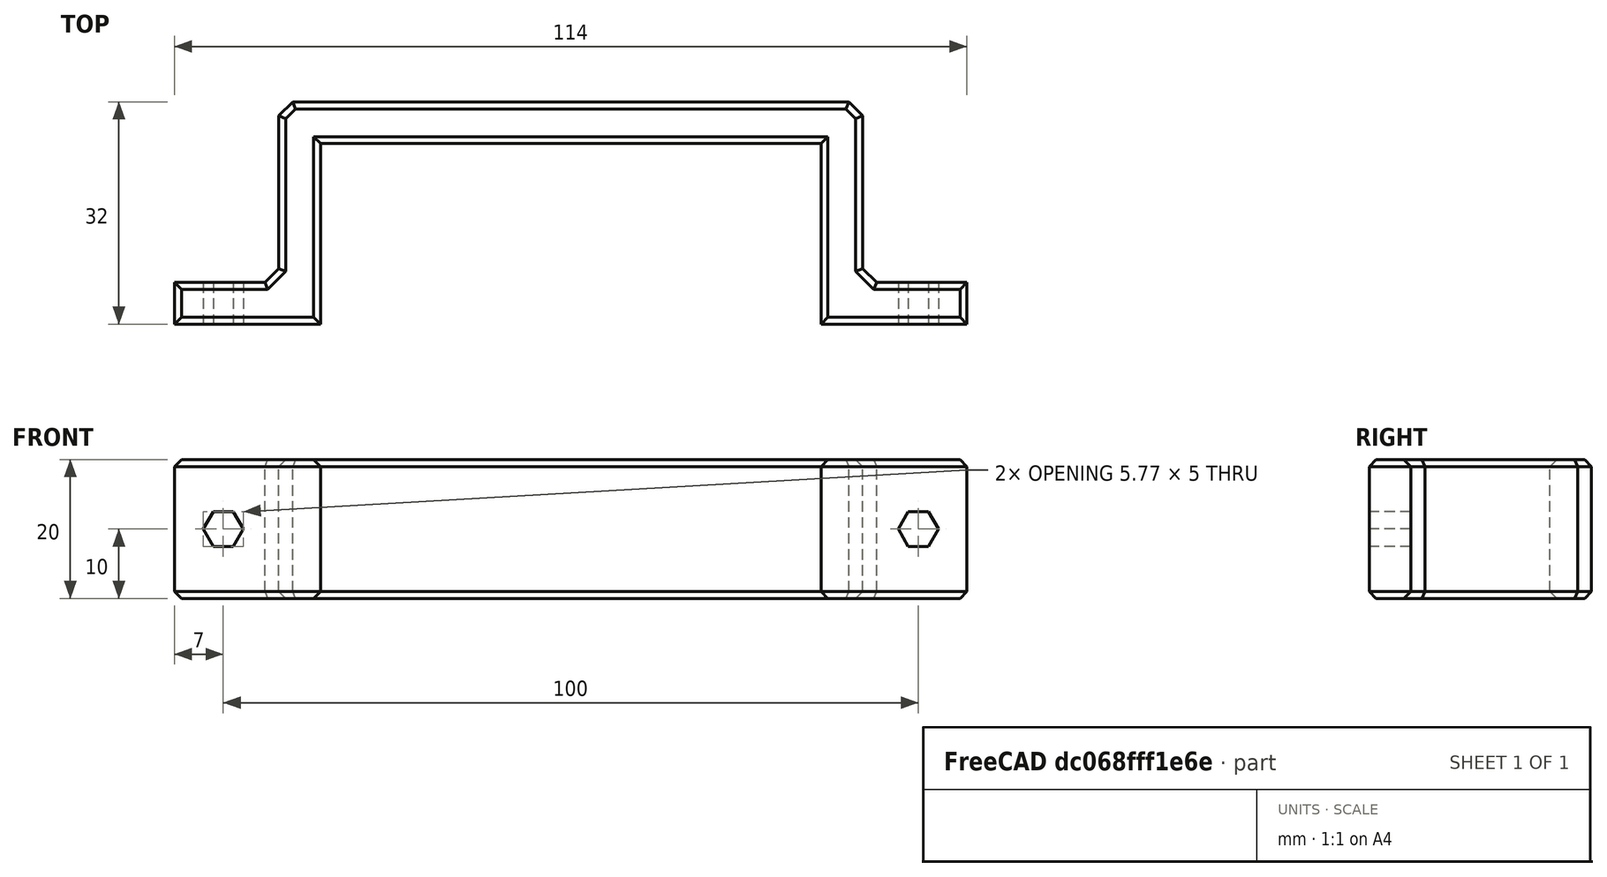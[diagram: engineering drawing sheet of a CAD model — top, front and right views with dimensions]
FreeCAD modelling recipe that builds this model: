
FCSTD DOCUMENT  (FreeCAD 0.19R)
Label: ChargerClip
License: All rights reserved
LicenseURL: http://en.wikipedia.org/wiki/All_rights_reserved
objects: PartDesign::Chamfer×3, Sketcher::SketchObject×2, PartDesign::Pad×1, PartDesign::Pocket×1, PartDesign::Body×1, Mesh::Feature×1
note: 13 computed .brp shape members not serialized (recipe doc carries the construction recipe); baked Part::Feature solids carry a one-line shape summary decoded from their .brp

FEATURE [Sketcher::SketchObject] Sketch
  FullyConstrained = true
  MapMode = 5
  Support = -> [XY_Plane]
  sketch-geometry (12):
    g0: LineSegment StartX=-57 StartY=0 StartZ=0 EndX=-57 EndY=6 EndZ=0
    g1: LineSegment StartX=-57 StartY=6 StartZ=0 EndX=-42 EndY=6 EndZ=0
    g2: LineSegment StartX=-42 StartY=6 StartZ=0 EndX=-42 EndY=32 EndZ=0
    g3: LineSegment StartX=-42 StartY=32 StartZ=0 EndX=42 EndY=32 EndZ=0
    g4: LineSegment StartX=42 StartY=32 StartZ=0 EndX=42 EndY=6 EndZ=0
    g5: LineSegment StartX=42 StartY=6 StartZ=0 EndX=57 EndY=6 EndZ=0
    g6: LineSegment StartX=57 StartY=6 StartZ=0 EndX=57 EndY=0 EndZ=0
    g7: LineSegment StartX=57 StartY=0 StartZ=0 EndX=36 EndY=0 EndZ=0
    g8: LineSegment StartX=36 StartY=0 StartZ=0 EndX=36 EndY=26 EndZ=0
    g9: LineSegment StartX=36 StartY=26 StartZ=0 EndX=-36 EndY=26 EndZ=0
    g10: LineSegment StartX=-36 StartY=26 StartZ=0 EndX=-36 EndY=0 EndZ=0
    g11: LineSegment StartX=-36 StartY=0 StartZ=0 EndX=-57 EndY=0 EndZ=0
  constraints (33):
    c: PointOnObject(g0,g-1)
    c: Vertical(g0)
    c: Coincident(g0,g1)
    c: Horizontal(g1)
    c: Coincident(g1,g2)
    c: Vertical(g2)
    c: Coincident(g2,g3)
    c: Coincident(g3,g4)
    c: Coincident(g4,g5)
    c: Horizontal(g5)
    c: Coincident(g5,g6)
    c: PointOnObject(g6,g-1)
    c: Coincident(g6,g7)
    c: PointOnObject(g7,g-1)
    c: Coincident(g7,g8)
    c: Vertical(g8)
    c: Coincident(g8,g9)
    c: Coincident(g9,g10)
    c: Coincident(g10,g11)
    c: Coincident(g11,g0)
    c: Symmetric(g8,g9,g-2)
    c: Symmetric(g3,g2,g-2)
    c: Symmetric(g7,g10,g-2)
    c: Distance(g10,g7) = 72
    c: Vertical(g4)
    c: Distance(g4,g8) = 6
    c: Distance(g9,g3) = 6
    c: Vertical(g6)
    c: Equal(g5,g1)
    c: Distance(g5) = 15
    c: Distance(g6) = 6
    c: Equal(g0,g6)
    c: Distance(g8) = 26
FEATURE [PartDesign::Pad] Pad
  Direction = (1,1,1)
  Length = 20
  Length2 = 100
  Profile = -> Sketch
  Type = 0
FEATURE [Sketcher::SketchObject] Sketch001
  FullyConstrained = true
  MapMode = 5
  Placement = pos=(0,6,0) rot=(0,0.707107,0.707107;3.14159rad)
  Support = -> [Pad]
  sketch-geometry (14):
    g0: LineSegment StartX=-48.5566 StartY=7.5 StartZ=0 EndX=-47.1132 EndY=10 EndZ=0
    g1: LineSegment StartX=-47.1132 StartY=10 StartZ=0 EndX=-48.5566 EndY=12.5 EndZ=0
    g2: LineSegment StartX=-48.5566 StartY=12.5 StartZ=0 EndX=-51.4434 EndY=12.5 EndZ=0
    g3: LineSegment StartX=-51.4434 StartY=12.5 StartZ=0 EndX=-52.8868 EndY=10 EndZ=0
    g4: LineSegment StartX=-52.8868 StartY=10 StartZ=0 EndX=-51.4434 EndY=7.5 EndZ=0
    g5: LineSegment StartX=-51.4434 StartY=7.5 StartZ=0 EndX=-48.5566 EndY=7.5 EndZ=0
    g6: Circle CenterX=-50 CenterY=10 CenterZ=0 NormalX=0 NormalY=0 NormalZ=1 AngleXU=0 Radius=2.88675
    g7: LineSegment StartX=51.4434 StartY=7.5 StartZ=0 EndX=52.8868 EndY=10 EndZ=0
    g8: LineSegment StartX=52.8868 StartY=10 StartZ=0 EndX=51.4434 EndY=12.5 EndZ=0
    g9: LineSegment StartX=51.4434 StartY=12.5 StartZ=0 EndX=48.5566 EndY=12.5 EndZ=0
    g10: LineSegment StartX=48.5566 StartY=12.5 StartZ=0 EndX=47.1132 EndY=10 EndZ=0
    g11: LineSegment StartX=47.1132 StartY=10 StartZ=0 EndX=48.5566 EndY=7.5 EndZ=0
    g12: LineSegment StartX=48.5566 StartY=7.5 StartZ=0 EndX=51.4434 EndY=7.5 EndZ=0
    g13: Circle CenterX=50 CenterY=10 CenterZ=0 NormalX=0 NormalY=0 NormalZ=1 AngleXU=0 Radius=2.88675
  constraints (33):
    c: Coincident(g0,g1)
    c: Coincident(g1,g2)
    c: Coincident(g2,g3)
    c: Coincident(g3,g4)
    c: Coincident(g4,g5)
    c: Coincident(g5,g0)
    c: Equal(g0, g1-g5) x5
    c: PointOnObject(g0,g6)
    c: PointOnObject(g1,g6)
    c: PointOnObject(g2,g6)
    c: PointOnObject(g3,g6)
    c: PointOnObject(g4,g6)
    c: PointOnObject(g5,g6)
    c: Coincident(g7,g8)
    c: Coincident(g8,g9)
    c: Coincident(g9,g10)
    c: Coincident(g10,g11)
    c: Coincident(g11,g12)
    c: Coincident(g12,g7)
    c: Equal(g7, g8-g12) x5
    c: PointOnObject(g7,g13)
    c: PointOnObject(g8,g13)
    c: PointOnObject(g9,g13)
    c: PointOnObject(g10,g13)
    c: PointOnObject(g11,g13)
    c: PointOnObject(g12,g13)
    c: Symmetric(g13,g6,g-2)
    c: Distance(g1,g0) = 5
    c: Equal(g1,g8)
    c: DistanceY(g6) = 10
    c: DistanceX(g6) = -50
    c: Horizontal(g2)
    c: Horizontal(g9)
FEATURE [PartDesign::Pocket] Pocket
  BaseFeature = -> Pad
  Length = 5
  Length2 = 100
  Profile = -> Sketch001
  Type = 1
FEATURE [PartDesign::Chamfer] Chamfer
  Angle = 45
  Base = -> Pocket [Edge48,Edge49,Edge16,Edge50]
  BaseFeature = -> Pocket
  ChamferType = 0
  FlipDirection = false
  Size = 2
  Size2 = 1
  SupportTransform = false
FEATURE [PartDesign::Chamfer] Chamfer001
  Angle = 45
  Base = -> Chamfer [Face2]
  BaseFeature = -> Chamfer
  ChamferType = 0
  FlipDirection = false
  Size = 1
  Size2 = 1
  SupportTransform = false
FEATURE [PartDesign::Chamfer] Chamfer002
  Angle = 45
  Base = -> Chamfer001 [Face4]
  BaseFeature = -> Chamfer001
  ChamferType = 0
  FlipDirection = false
  Size = 1
  Size2 = 1
  SupportTransform = false
FEATURE [PartDesign::Body] Body
  Group = -> [Sketch,Pad,Sketch001,Pocket,Chamfer,Chamfer001,Chamfer002]
  Origin = -> Origin
  Tip = -> Chamfer002
FEATURE [Mesh::Feature] Mesh  label="Chamfer002 (Meshed)"
